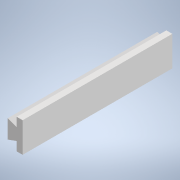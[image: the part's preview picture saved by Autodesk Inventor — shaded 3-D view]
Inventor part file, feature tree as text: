
AUTODESK INVENTOR PART (.ipt)
format: ipt  version: 2021 (Build 250183000, 183)  size: 154,112 bytes
history: native  units: mm
features: sketch x4, extrude x4, other x2, plane x1, reference x1, projected_geometry x1
ambient origin geometry x8: Origin, YZ Plane, XZ Plane, XY Plane, X Axis, Y Axis, Z Axis, Center Point
bodies: Solid1 (feature_tree)
feature tree (13):
  sketch  "Sketch1"  dims[d0=10.0mm d1=10.0mm d2=0.0mm]
  plane  "Work Plane1"
  extrude  "Extrusion1"  Depth=10.0mm TaperAngle=0.0deg
  extrude  "Extrusion2"  Depth=20.0mm
  extrude  "Extrusion3"  Depth=3.0mm
  extrude  "Extrusion4"  Depth=10.0mm
  reference  "Reference1"
  sketch  "Sketch2"  dims[d3=14.0mm d4=20.0mm]
  projected_geometry  "Projected Loop1"
  sketch  "Sketch3"  dims[d5=3.0mm d6=0.0mm d7=3.0mm]
  sketch  "Sketch4"  dims[d8=6.0mm d9=120.0mm d11=8.0mm d12=10.0mm d14=10.0mm d16=0.0mm d17=0.0mm d18=5.5mm d19=5.5mm d20=7.0mm d21=0.0mm]
  other  "Assembly1"
  other  "prismatic link inner:5"
